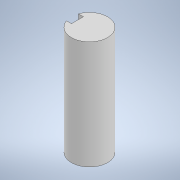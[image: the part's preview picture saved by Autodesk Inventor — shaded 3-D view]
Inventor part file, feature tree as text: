
AUTODESK INVENTOR PART (.ipt)
format: ipt  version: 2022 (Build 260153000, 153)  size: 97,280 bytes
history: native  units: mm
features: extrude x1, sketch x1
ambient origin geometry x8: Origin, YZ Plane, XZ Plane, XY Plane, X Axis, Y Axis, Z Axis, Center Point
bodies: Solid1 (feature_tree)
feature tree (2):
  extrude  "Extrusion1"  Depth=5.0mm
  sketch  "Sketch1"  dims[d0=15.0mm d1=5.0mm d2=5.0mm d3=45.0mm d4=0.0mm]
